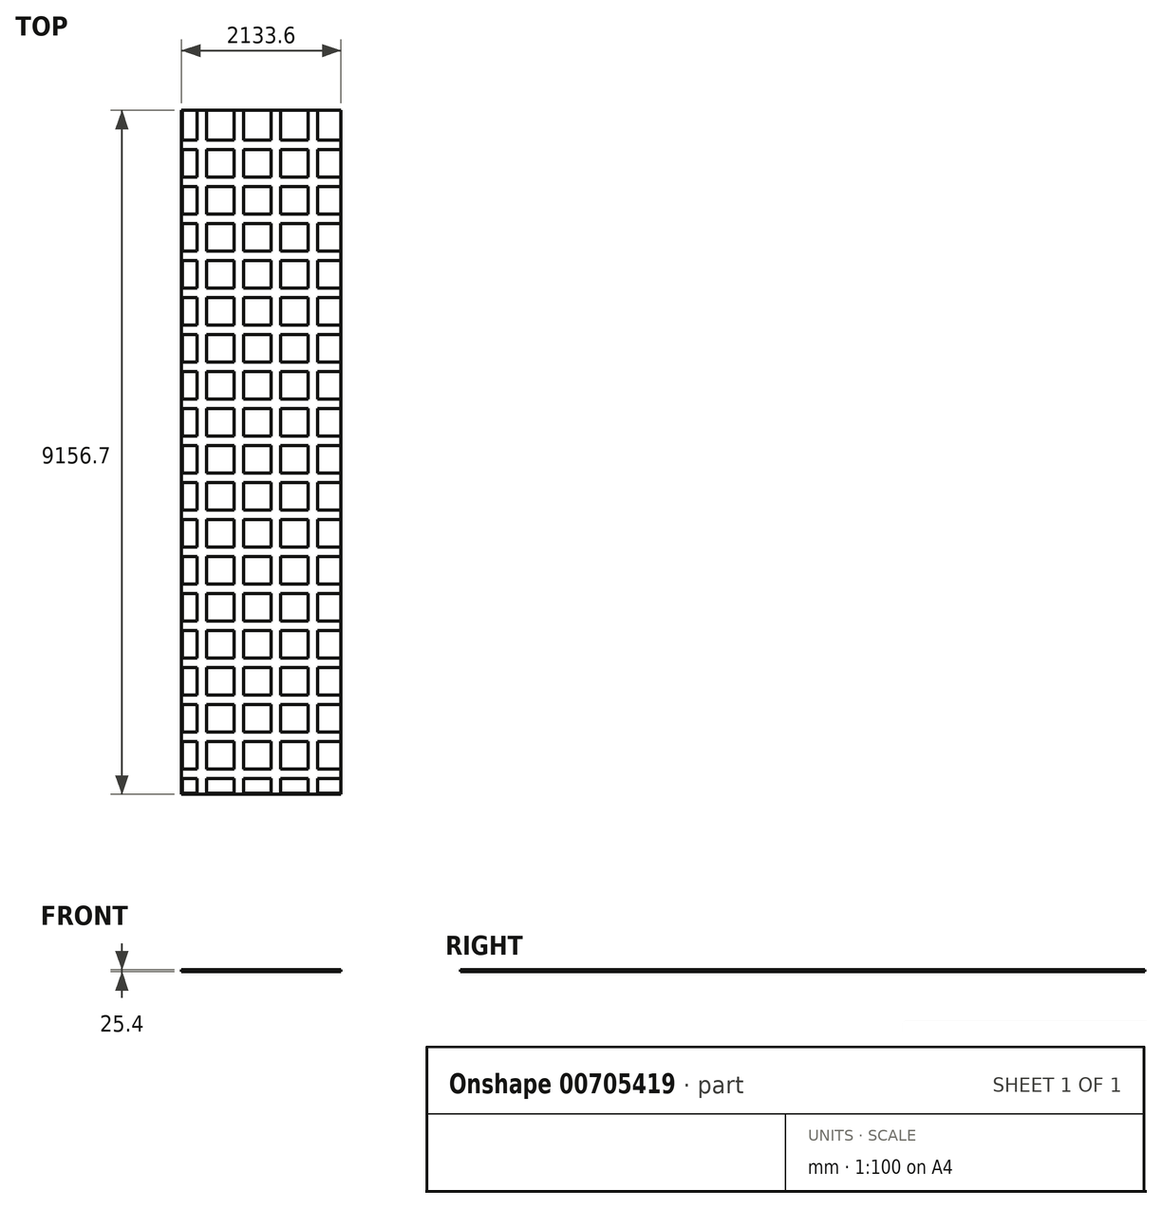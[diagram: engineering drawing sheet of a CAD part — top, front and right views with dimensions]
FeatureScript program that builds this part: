
annotation { "Feature Type Name" : "Feature", "Feature Type Description" : "" }
export const myFeature = defineFeature(function(context is Context, id is Id, definition is map)
    precondition{}
    {
        {
            var Q0;
            Q0=qCreatedBy(makeId("Top.planeOp"),FACE);
            var sketch = newSketch(context, id + "F0", { "sketchPlane" : qUnion([Q0])});
            skLineSegment(sketch, "E0.bottom", {"start": v(0, 0) * mm, "end": v(2133.6, 0) * mm});
            skLineSegment(sketch, "E0.top", {"start": v(0, 9156.7) * mm, "end": v(2133.6, 9156.7) * mm});
            skLineSegment(sketch, "E0.left", {"start": v(0, 0) * mm, "end": v(0, 9156.7) * mm});
            skLineSegment(sketch, "E0.right", {"start": v(2133.6, 0) * mm, "end": v(2133.6, 9156.7) * mm});
            skSolve(sketch);
        }
        {
            var Q0;
            Q0=makeQuery(id+"F0.imprint","IMPRINT",FACE,{"disambiguationData":[TD([[makeQuery(id+"F0.imprint","IMPRINT",EDGE,{"derivedFrom":sQuery(id+"F0.wireOp",EDGE,"E0.bottom")}),1.0]])]});
            extrude(context, id + "F1", {"entities" : qUnion([Q0]), "depth" : 25.4 * mm, "offsetDistance" : 25.4 * mm});
        }
        {
            var Q0;
            Q0=makeQuery(id+"F1.opExtrude","CAP_FACE",FACE,{"disambiguationData":[OSD([sQuery(id+"F0.wireOp",EDGE,"E0.bottom"),sQuery(id+"F0.wireOp",EDGE,"E0.top"),sQuery(id+"F0.wireOp",EDGE,"E0.left"),sQuery(id+"F0.wireOp",EDGE,"E0.right")])],"isStart":false});
            var sketch = newSketch(context, id + "F2", { "sketchPlane" : qUnion([Q0])});
            skLineSegment(sketch, "E1.0", {"start": v(12.7, 0) * mm, "end": v(12.7, 9156.7) * mm});
            skLineSegment(sketch, "E2", {"start": v(336.55, 12.7) * mm, "end": v(336.55, 9156.7) * mm});
            skLineSegment(sketch, "E3.0", {"start": v(0, 12.7) * mm, "end": v(2133.6, 12.7) * mm});
            skLineSegment(sketch, "E4", {"start": v(12.7, 336.55) * mm, "end": v(2133.6, 336.55) * mm});
            skLineSegment(sketch, "E5.0", {"start": v(209.55, 12.7) * mm, "end": v(209.55, 9156.7) * mm});
            skLineSegment(sketch, "E6.0", {"start": v(12.7, 209.55) * mm, "end": v(2133.6, 209.55) * mm});
            skLineSegment(sketch, "E7.1.0.0", {"start": v(704.85, 12.7) * mm, "end": v(704.85, 9156.7) * mm});
            skLineSegment(sketch, "E7.1.0.1", {"start": v(831.85, 12.7) * mm, "end": v(831.85, 9156.7) * mm});
            skLineSegment(sketch, "E7.2.0.0", {"start": v(1200.15, 12.7) * mm, "end": v(1200.15, 9156.7) * mm});
            skLineSegment(sketch, "E7.2.0.1", {"start": v(1327.15, 12.7) * mm, "end": v(1327.15, 9156.7) * mm});
            skLineSegment(sketch, "E7.3.0.0", {"start": v(1695.45, 12.7) * mm, "end": v(1695.45, 9156.7) * mm});
            skLineSegment(sketch, "E7.3.0.1", {"start": v(1822.45, 12.7) * mm, "end": v(1822.45, 9156.7) * mm});
            skLineSegment(sketch, "E7.direction1", {"start": v(209.55, 12.7) * mm, "end": v(704.85, 12.7) * mm, "construction": true});
            skLineSegment(sketch, "E8.0.1.0", {"start": v(12.7, 831.85) * mm, "end": v(2133.6, 831.85) * mm});
            skLineSegment(sketch, "E8.0.1.1", {"start": v(12.7, 704.85) * mm, "end": v(2133.6, 704.85) * mm});
            skLineSegment(sketch, "E8.0.2.0", {"start": v(12.7, 1327.15) * mm, "end": v(2133.6, 1327.15) * mm});
            skLineSegment(sketch, "E8.0.2.1", {"start": v(12.7, 1200.15) * mm, "end": v(2133.6, 1200.15) * mm});
            skLineSegment(sketch, "E8.0.3.0", {"start": v(12.7, 1822.45) * mm, "end": v(2133.6, 1822.45) * mm});
            skLineSegment(sketch, "E8.0.3.1", {"start": v(12.7, 1695.45) * mm, "end": v(2133.6, 1695.45) * mm});
            skLineSegment(sketch, "E8.0.4.0", {"start": v(12.7, 2317.75) * mm, "end": v(2133.6, 2317.75) * mm});
            skLineSegment(sketch, "E8.0.4.1", {"start": v(12.7, 2190.75) * mm, "end": v(2133.6, 2190.75) * mm});
            skLineSegment(sketch, "E8.0.5.0", {"start": v(12.7, 2813.05) * mm, "end": v(2133.6, 2813.05) * mm});
            skLineSegment(sketch, "E8.0.5.1", {"start": v(12.7, 2686.05) * mm, "end": v(2133.6, 2686.05) * mm});
            skLineSegment(sketch, "E8.0.6.0", {"start": v(12.7, 3308.35) * mm, "end": v(2133.6, 3308.35) * mm});
            skLineSegment(sketch, "E8.0.6.1", {"start": v(12.7, 3181.35) * mm, "end": v(2133.6, 3181.35) * mm});
            skLineSegment(sketch, "E8.0.7.0", {"start": v(12.7, 3803.65) * mm, "end": v(2133.6, 3803.65) * mm});
            skLineSegment(sketch, "E8.0.7.1", {"start": v(12.7, 3676.65) * mm, "end": v(2133.6, 3676.65) * mm});
            skLineSegment(sketch, "E8.0.8.0", {"start": v(12.7, 4298.95) * mm, "end": v(2133.6, 4298.95) * mm});
            skLineSegment(sketch, "E8.0.8.1", {"start": v(12.7, 4171.95) * mm, "end": v(2133.6, 4171.95) * mm});
            skLineSegment(sketch, "E8.0.9.0", {"start": v(12.7, 4794.25) * mm, "end": v(2133.6, 4794.25) * mm});
            skLineSegment(sketch, "E8.0.9.1", {"start": v(12.7, 4667.25) * mm, "end": v(2133.6, 4667.25) * mm});
            skLineSegment(sketch, "E8.0.10.0", {"start": v(12.7, 5289.55) * mm, "end": v(2133.6, 5289.55) * mm});
            skLineSegment(sketch, "E8.0.10.1", {"start": v(12.7, 5162.55) * mm, "end": v(2133.6, 5162.55) * mm});
            skLineSegment(sketch, "E8.0.11.0", {"start": v(12.7, 5784.85) * mm, "end": v(2133.6, 5784.85) * mm});
            skLineSegment(sketch, "E8.0.11.1", {"start": v(12.7, 5657.85) * mm, "end": v(2133.6, 5657.85) * mm});
            skLineSegment(sketch, "E8.0.12.0", {"start": v(12.7, 6280.15) * mm, "end": v(2133.6, 6280.15) * mm});
            skLineSegment(sketch, "E8.0.12.1", {"start": v(12.7, 6153.15) * mm, "end": v(2133.6, 6153.15) * mm});
            skLineSegment(sketch, "E8.0.13.0", {"start": v(12.7, 6775.45) * mm, "end": v(2133.6, 6775.45) * mm});
            skLineSegment(sketch, "E8.0.13.1", {"start": v(12.7, 6648.45) * mm, "end": v(2133.6, 6648.45) * mm});
            skLineSegment(sketch, "E8.0.14.0", {"start": v(12.7, 7270.75) * mm, "end": v(2133.6, 7270.75) * mm});
            skLineSegment(sketch, "E8.0.14.1", {"start": v(12.7, 7143.75) * mm, "end": v(2133.6, 7143.75) * mm});
            skLineSegment(sketch, "E8.0.15.0", {"start": v(12.7, 7766.05) * mm, "end": v(2133.6, 7766.05) * mm});
            skLineSegment(sketch, "E8.0.15.1", {"start": v(12.7, 7639.05) * mm, "end": v(2133.6, 7639.05) * mm});
            skLineSegment(sketch, "E8.0.16.0", {"start": v(12.7, 8261.35) * mm, "end": v(2133.6, 8261.35) * mm});
            skLineSegment(sketch, "E8.0.16.1", {"start": v(12.7, 8134.35) * mm, "end": v(2133.6, 8134.35) * mm});
            skLineSegment(sketch, "E8.0.17.0", {"start": v(12.7, 8756.65) * mm, "end": v(2133.6, 8756.65) * mm});
            skLineSegment(sketch, "E8.0.17.1", {"start": v(12.7, 8629.65) * mm, "end": v(2133.6, 8629.65) * mm});
            skLineSegment(sketch, "E8.direction1", {"start": v(12.7, 336.55) * mm, "end": v(38.1, 336.55) * mm, "construction": true});
            skLineSegment(sketch, "E8.direction2", {"start": v(12.7, 336.55) * mm, "end": v(12.7, 831.85) * mm, "construction": true});
            skLineSegment(sketch, "E9.3.0.18", {"start": v(12.7, 9124.95) * mm, "end": v(2133.6, 9124.95) * mm});
            skSolve(sketch);
        }
        {
            var Q0;
            {var subQ0=sQuery(id+"F2.wireOp",EDGE,"E4");var subQ1=sQuery(id+"F2.wireOp",EDGE,"E1.0");var subQ2=makeQuery(id+"F2.imprint","INTERSECT",VERTEX,{"derivedFrom":[subQ1,subQ0]});Q0=makeQuery(id+"F2.imprint","IMPRINT",FACE,{"disambiguationData":[TD([[makeQuery(id+"F2.imprint","IMPRINT",EDGE,{"disambiguationData":[TD([[subQ2,-1.0]])],"derivedFrom":subQ1}),-1.0]])]});}
            var Q1;
            {var subQ0=sQuery(id+"F2.wireOp",EDGE,"E4");var subQ1=sQuery(id+"F2.wireOp",EDGE,"E2");var subQ2=makeQuery(id+"F2.imprint","INTERSECT",VERTEX,{"derivedFrom":[subQ1,subQ0]});Q1=makeQuery(id+"F2.imprint","IMPRINT",FACE,{"disambiguationData":[TD([[makeQuery(id+"F2.imprint","IMPRINT",EDGE,{"disambiguationData":[TD([[subQ2,-1.0]])],"derivedFrom":subQ1}),-1.0]])]});}
            var Q2;
            {var subQ0=sQuery(id+"F2.wireOp",EDGE,"E7.1.0.1");var subQ1=sQuery(id+"F2.wireOp",EDGE,"E4");var subQ2=makeQuery(id+"F2.imprint","INTERSECT",VERTEX,{"derivedFrom":[subQ1,subQ0]});Q2=makeQuery(id+"F2.imprint","IMPRINT",FACE,{"disambiguationData":[TD([[makeQuery(id+"F2.imprint","IMPRINT",EDGE,{"disambiguationData":[TD([[subQ2,-1.0]])],"derivedFrom":subQ1}),1.0]])]});}
            var Q3;
            {var subQ0=sQuery(id+"F2.wireOp",EDGE,"E7.2.0.1");var subQ1=sQuery(id+"F2.wireOp",EDGE,"E4");var subQ2=makeQuery(id+"F2.imprint","INTERSECT",VERTEX,{"derivedFrom":[subQ1,subQ0]});Q3=makeQuery(id+"F2.imprint","IMPRINT",FACE,{"disambiguationData":[TD([[makeQuery(id+"F2.imprint","IMPRINT",EDGE,{"disambiguationData":[TD([[subQ2,-1.0]])],"derivedFrom":subQ1}),1.0]])]});}
            var Q4;
            {var subQ0=sQuery(id+"F2.wireOp",EDGE,"E4");var subQ1=makeQuery(id+"F1.opExtrude","CAP_EDGE",EDGE,{"disambiguationData":[OSD([sQuery(id+"F0.wireOp",EDGE,"E0.right")])],"isStart":false});var subQ2=makeQuery(id+"F2.imprint","INTERSECT",VERTEX,{"derivedFrom":[subQ1,subQ0]});Q4=makeQuery(id+"F2.imprint","IMPRINT",FACE,{"disambiguationData":[TD([[makeQuery(id+"F2.imprint","IMPRINT",EDGE,{"disambiguationData":[TD([[subQ2,1.0]])],"derivedFrom":subQ0}),1.0]])]});}
            var Q5;
            {var subQ0=sQuery(id+"F2.wireOp",EDGE,"E8.0.1.0");var subQ1=sQuery(id+"F2.wireOp",EDGE,"E1.0");var subQ2=makeQuery(id+"F2.imprint","INTERSECT",VERTEX,{"derivedFrom":[subQ1,subQ0]});Q5=makeQuery(id+"F2.imprint","IMPRINT",FACE,{"disambiguationData":[TD([[makeQuery(id+"F2.imprint","IMPRINT",EDGE,{"disambiguationData":[TD([[subQ2,-1.0]])],"derivedFrom":subQ1}),-1.0]])]});}
            var Q6;
            {var subQ0=sQuery(id+"F2.wireOp",EDGE,"E8.0.1.0");var subQ1=sQuery(id+"F2.wireOp",EDGE,"E2");var subQ2=makeQuery(id+"F2.imprint","INTERSECT",VERTEX,{"derivedFrom":[subQ1,subQ0]});Q6=makeQuery(id+"F2.imprint","IMPRINT",FACE,{"disambiguationData":[TD([[makeQuery(id+"F2.imprint","IMPRINT",EDGE,{"disambiguationData":[TD([[subQ2,-1.0]])],"derivedFrom":subQ1}),-1.0]])]});}
            var Q7;
            {var subQ0=sQuery(id+"F2.wireOp",EDGE,"E8.0.1.0");var subQ1=sQuery(id+"F2.wireOp",EDGE,"E7.1.0.1");var subQ2=makeQuery(id+"F2.imprint","INTERSECT",VERTEX,{"derivedFrom":[subQ1,subQ0]});Q7=makeQuery(id+"F2.imprint","IMPRINT",FACE,{"disambiguationData":[TD([[makeQuery(id+"F2.imprint","IMPRINT",EDGE,{"disambiguationData":[TD([[subQ2,-1.0]])],"derivedFrom":subQ1}),-1.0]])]});}
            var Q8;
            {var subQ0=sQuery(id+"F2.wireOp",EDGE,"E8.0.1.0");var subQ1=sQuery(id+"F2.wireOp",EDGE,"E7.2.0.1");var subQ2=makeQuery(id+"F2.imprint","INTERSECT",VERTEX,{"derivedFrom":[subQ1,subQ0]});Q8=makeQuery(id+"F2.imprint","IMPRINT",FACE,{"disambiguationData":[TD([[makeQuery(id+"F2.imprint","IMPRINT",EDGE,{"disambiguationData":[TD([[subQ2,-1.0]])],"derivedFrom":subQ1}),-1.0]])]});}
            var Q9;
            {var subQ0=sQuery(id+"F2.wireOp",EDGE,"E8.0.1.0");var subQ1=sQuery(id+"F2.wireOp",EDGE,"E7.3.0.1");var subQ2=makeQuery(id+"F2.imprint","INTERSECT",VERTEX,{"derivedFrom":[subQ1,subQ0]});Q9=makeQuery(id+"F2.imprint","IMPRINT",FACE,{"disambiguationData":[TD([[makeQuery(id+"F2.imprint","IMPRINT",EDGE,{"disambiguationData":[TD([[subQ2,-1.0]])],"derivedFrom":subQ1}),-1.0]])]});}
            var Q10;
            {var subQ0=sQuery(id+"F2.wireOp",EDGE,"E8.0.2.0");var subQ1=sQuery(id+"F2.wireOp",EDGE,"E7.3.0.1");var subQ2=makeQuery(id+"F2.imprint","INTERSECT",VERTEX,{"derivedFrom":[subQ1,subQ0]});Q10=makeQuery(id+"F2.imprint","IMPRINT",FACE,{"disambiguationData":[TD([[makeQuery(id+"F2.imprint","IMPRINT",EDGE,{"disambiguationData":[TD([[subQ2,-1.0]])],"derivedFrom":subQ1}),-1.0]])]});}
            var Q11;
            {var subQ0=sQuery(id+"F2.wireOp",EDGE,"E8.0.2.0");var subQ1=sQuery(id+"F2.wireOp",EDGE,"E7.2.0.1");var subQ2=makeQuery(id+"F2.imprint","INTERSECT",VERTEX,{"derivedFrom":[subQ1,subQ0]});Q11=makeQuery(id+"F2.imprint","IMPRINT",FACE,{"disambiguationData":[TD([[makeQuery(id+"F2.imprint","IMPRINT",EDGE,{"disambiguationData":[TD([[subQ2,-1.0]])],"derivedFrom":subQ1}),-1.0]])]});}
            var Q12;
            {var subQ0=sQuery(id+"F2.wireOp",EDGE,"E8.0.2.0");var subQ1=sQuery(id+"F2.wireOp",EDGE,"E7.1.0.1");var subQ2=makeQuery(id+"F2.imprint","INTERSECT",VERTEX,{"derivedFrom":[subQ1,subQ0]});Q12=makeQuery(id+"F2.imprint","IMPRINT",FACE,{"disambiguationData":[TD([[makeQuery(id+"F2.imprint","IMPRINT",EDGE,{"disambiguationData":[TD([[subQ2,-1.0]])],"derivedFrom":subQ1}),-1.0]])]});}
            var Q13;
            {var subQ0=sQuery(id+"F2.wireOp",EDGE,"E8.0.2.0");var subQ1=sQuery(id+"F2.wireOp",EDGE,"E2");var subQ2=makeQuery(id+"F2.imprint","INTERSECT",VERTEX,{"derivedFrom":[subQ1,subQ0]});Q13=makeQuery(id+"F2.imprint","IMPRINT",FACE,{"disambiguationData":[TD([[makeQuery(id+"F2.imprint","IMPRINT",EDGE,{"disambiguationData":[TD([[subQ2,-1.0]])],"derivedFrom":subQ1}),-1.0]])]});}
            var Q14;
            {var subQ0=sQuery(id+"F2.wireOp",EDGE,"E8.0.2.0");var subQ1=sQuery(id+"F2.wireOp",EDGE,"E1.0");var subQ2=makeQuery(id+"F2.imprint","INTERSECT",VERTEX,{"derivedFrom":[subQ1,subQ0]});Q14=makeQuery(id+"F2.imprint","IMPRINT",FACE,{"disambiguationData":[TD([[makeQuery(id+"F2.imprint","IMPRINT",EDGE,{"disambiguationData":[TD([[subQ2,-1.0]])],"derivedFrom":subQ1}),-1.0]])]});}
            var Q15;
            {var subQ0=sQuery(id+"F2.wireOp",EDGE,"E8.0.3.0");var subQ1=sQuery(id+"F2.wireOp",EDGE,"E1.0");var subQ2=makeQuery(id+"F2.imprint","INTERSECT",VERTEX,{"derivedFrom":[subQ1,subQ0]});Q15=makeQuery(id+"F2.imprint","IMPRINT",FACE,{"disambiguationData":[TD([[makeQuery(id+"F2.imprint","IMPRINT",EDGE,{"disambiguationData":[TD([[subQ2,-1.0]])],"derivedFrom":subQ1}),-1.0]])]});}
            var Q16;
            {var subQ0=sQuery(id+"F2.wireOp",EDGE,"E8.0.3.0");var subQ1=sQuery(id+"F2.wireOp",EDGE,"E2");var subQ2=makeQuery(id+"F2.imprint","INTERSECT",VERTEX,{"derivedFrom":[subQ1,subQ0]});Q16=makeQuery(id+"F2.imprint","IMPRINT",FACE,{"disambiguationData":[TD([[makeQuery(id+"F2.imprint","IMPRINT",EDGE,{"disambiguationData":[TD([[subQ2,-1.0]])],"derivedFrom":subQ1}),-1.0]])]});}
            var Q17;
            {var subQ0=sQuery(id+"F2.wireOp",EDGE,"E8.0.3.0");var subQ1=sQuery(id+"F2.wireOp",EDGE,"E7.1.0.1");var subQ2=makeQuery(id+"F2.imprint","INTERSECT",VERTEX,{"derivedFrom":[subQ1,subQ0]});Q17=makeQuery(id+"F2.imprint","IMPRINT",FACE,{"disambiguationData":[TD([[makeQuery(id+"F2.imprint","IMPRINT",EDGE,{"disambiguationData":[TD([[subQ2,-1.0]])],"derivedFrom":subQ1}),-1.0]])]});}
            var Q18;
            {var subQ0=sQuery(id+"F2.wireOp",EDGE,"E8.0.3.0");var subQ1=sQuery(id+"F2.wireOp",EDGE,"E7.2.0.1");var subQ2=makeQuery(id+"F2.imprint","INTERSECT",VERTEX,{"derivedFrom":[subQ1,subQ0]});Q18=makeQuery(id+"F2.imprint","IMPRINT",FACE,{"disambiguationData":[TD([[makeQuery(id+"F2.imprint","IMPRINT",EDGE,{"disambiguationData":[TD([[subQ2,-1.0]])],"derivedFrom":subQ1}),-1.0]])]});}
            var Q19;
            {var subQ0=sQuery(id+"F2.wireOp",EDGE,"E8.0.3.0");var subQ1=sQuery(id+"F2.wireOp",EDGE,"E7.3.0.1");var subQ2=makeQuery(id+"F2.imprint","INTERSECT",VERTEX,{"derivedFrom":[subQ1,subQ0]});Q19=makeQuery(id+"F2.imprint","IMPRINT",FACE,{"disambiguationData":[TD([[makeQuery(id+"F2.imprint","IMPRINT",EDGE,{"disambiguationData":[TD([[subQ2,-1.0]])],"derivedFrom":subQ1}),-1.0]])]});}
            var Q20;
            {var subQ0=sQuery(id+"F2.wireOp",EDGE,"E8.0.4.0");var subQ1=sQuery(id+"F2.wireOp",EDGE,"E7.3.0.1");var subQ2=makeQuery(id+"F2.imprint","INTERSECT",VERTEX,{"derivedFrom":[subQ1,subQ0]});Q20=makeQuery(id+"F2.imprint","IMPRINT",FACE,{"disambiguationData":[TD([[makeQuery(id+"F2.imprint","IMPRINT",EDGE,{"disambiguationData":[TD([[subQ2,-1.0]])],"derivedFrom":subQ1}),-1.0]])]});}
            var Q21;
            {var subQ0=sQuery(id+"F2.wireOp",EDGE,"E8.0.4.0");var subQ1=sQuery(id+"F2.wireOp",EDGE,"E7.2.0.1");var subQ2=makeQuery(id+"F2.imprint","INTERSECT",VERTEX,{"derivedFrom":[subQ1,subQ0]});Q21=makeQuery(id+"F2.imprint","IMPRINT",FACE,{"disambiguationData":[TD([[makeQuery(id+"F2.imprint","IMPRINT",EDGE,{"disambiguationData":[TD([[subQ2,-1.0]])],"derivedFrom":subQ1}),-1.0]])]});}
            var Q22;
            {var subQ0=sQuery(id+"F2.wireOp",EDGE,"E8.0.4.0");var subQ1=sQuery(id+"F2.wireOp",EDGE,"E7.1.0.1");var subQ2=makeQuery(id+"F2.imprint","INTERSECT",VERTEX,{"derivedFrom":[subQ1,subQ0]});Q22=makeQuery(id+"F2.imprint","IMPRINT",FACE,{"disambiguationData":[TD([[makeQuery(id+"F2.imprint","IMPRINT",EDGE,{"disambiguationData":[TD([[subQ2,-1.0]])],"derivedFrom":subQ1}),-1.0]])]});}
            var Q23;
            {var subQ0=sQuery(id+"F2.wireOp",EDGE,"E8.0.4.0");var subQ1=sQuery(id+"F2.wireOp",EDGE,"E2");var subQ2=makeQuery(id+"F2.imprint","INTERSECT",VERTEX,{"derivedFrom":[subQ1,subQ0]});Q23=makeQuery(id+"F2.imprint","IMPRINT",FACE,{"disambiguationData":[TD([[makeQuery(id+"F2.imprint","IMPRINT",EDGE,{"disambiguationData":[TD([[subQ2,-1.0]])],"derivedFrom":subQ1}),-1.0]])]});}
            var Q24;
            {var subQ0=sQuery(id+"F2.wireOp",EDGE,"E8.0.4.0");var subQ1=sQuery(id+"F2.wireOp",EDGE,"E1.0");var subQ2=makeQuery(id+"F2.imprint","INTERSECT",VERTEX,{"derivedFrom":[subQ1,subQ0]});Q24=makeQuery(id+"F2.imprint","IMPRINT",FACE,{"disambiguationData":[TD([[makeQuery(id+"F2.imprint","IMPRINT",EDGE,{"disambiguationData":[TD([[subQ2,-1.0]])],"derivedFrom":subQ1}),-1.0]])]});}
            var Q25;
            {var subQ0=sQuery(id+"F2.wireOp",EDGE,"E8.0.5.0");var subQ1=sQuery(id+"F2.wireOp",EDGE,"E1.0");var subQ2=makeQuery(id+"F2.imprint","INTERSECT",VERTEX,{"derivedFrom":[subQ1,subQ0]});Q25=makeQuery(id+"F2.imprint","IMPRINT",FACE,{"disambiguationData":[TD([[makeQuery(id+"F2.imprint","IMPRINT",EDGE,{"disambiguationData":[TD([[subQ2,-1.0]])],"derivedFrom":subQ1}),-1.0]])]});}
            var Q26;
            {var subQ0=sQuery(id+"F2.wireOp",EDGE,"E8.0.5.0");var subQ1=sQuery(id+"F2.wireOp",EDGE,"E2");var subQ2=makeQuery(id+"F2.imprint","INTERSECT",VERTEX,{"derivedFrom":[subQ1,subQ0]});Q26=makeQuery(id+"F2.imprint","IMPRINT",FACE,{"disambiguationData":[TD([[makeQuery(id+"F2.imprint","IMPRINT",EDGE,{"disambiguationData":[TD([[subQ2,-1.0]])],"derivedFrom":subQ1}),-1.0]])]});}
            var Q27;
            {var subQ0=sQuery(id+"F2.wireOp",EDGE,"E8.0.5.0");var subQ1=sQuery(id+"F2.wireOp",EDGE,"E7.1.0.1");var subQ2=makeQuery(id+"F2.imprint","INTERSECT",VERTEX,{"derivedFrom":[subQ1,subQ0]});Q27=makeQuery(id+"F2.imprint","IMPRINT",FACE,{"disambiguationData":[TD([[makeQuery(id+"F2.imprint","IMPRINT",EDGE,{"disambiguationData":[TD([[subQ2,-1.0]])],"derivedFrom":subQ1}),-1.0]])]});}
            var Q28;
            {var subQ0=sQuery(id+"F2.wireOp",EDGE,"E8.0.5.0");var subQ1=sQuery(id+"F2.wireOp",EDGE,"E7.2.0.1");var subQ2=makeQuery(id+"F2.imprint","INTERSECT",VERTEX,{"derivedFrom":[subQ1,subQ0]});Q28=makeQuery(id+"F2.imprint","IMPRINT",FACE,{"disambiguationData":[TD([[makeQuery(id+"F2.imprint","IMPRINT",EDGE,{"disambiguationData":[TD([[subQ2,-1.0]])],"derivedFrom":subQ1}),-1.0]])]});}
            var Q29;
            {var subQ0=sQuery(id+"F2.wireOp",EDGE,"E8.0.5.0");var subQ1=sQuery(id+"F2.wireOp",EDGE,"E7.3.0.1");var subQ2=makeQuery(id+"F2.imprint","INTERSECT",VERTEX,{"derivedFrom":[subQ1,subQ0]});Q29=makeQuery(id+"F2.imprint","IMPRINT",FACE,{"disambiguationData":[TD([[makeQuery(id+"F2.imprint","IMPRINT",EDGE,{"disambiguationData":[TD([[subQ2,-1.0]])],"derivedFrom":subQ1}),-1.0]])]});}
            var Q30;
            {var subQ0=sQuery(id+"F2.wireOp",EDGE,"E8.0.6.0");var subQ1=sQuery(id+"F2.wireOp",EDGE,"E7.3.0.1");var subQ2=makeQuery(id+"F2.imprint","INTERSECT",VERTEX,{"derivedFrom":[subQ1,subQ0]});Q30=makeQuery(id+"F2.imprint","IMPRINT",FACE,{"disambiguationData":[TD([[makeQuery(id+"F2.imprint","IMPRINT",EDGE,{"disambiguationData":[TD([[subQ2,-1.0]])],"derivedFrom":subQ1}),-1.0]])]});}
            var Q31;
            {var subQ0=sQuery(id+"F2.wireOp",EDGE,"E8.0.6.0");var subQ1=sQuery(id+"F2.wireOp",EDGE,"E7.2.0.1");var subQ2=makeQuery(id+"F2.imprint","INTERSECT",VERTEX,{"derivedFrom":[subQ1,subQ0]});Q31=makeQuery(id+"F2.imprint","IMPRINT",FACE,{"disambiguationData":[TD([[makeQuery(id+"F2.imprint","IMPRINT",EDGE,{"disambiguationData":[TD([[subQ2,-1.0]])],"derivedFrom":subQ1}),-1.0]])]});}
            var Q32;
            {var subQ0=sQuery(id+"F2.wireOp",EDGE,"E8.0.6.0");var subQ1=sQuery(id+"F2.wireOp",EDGE,"E7.1.0.1");var subQ2=makeQuery(id+"F2.imprint","INTERSECT",VERTEX,{"derivedFrom":[subQ1,subQ0]});Q32=makeQuery(id+"F2.imprint","IMPRINT",FACE,{"disambiguationData":[TD([[makeQuery(id+"F2.imprint","IMPRINT",EDGE,{"disambiguationData":[TD([[subQ2,-1.0]])],"derivedFrom":subQ1}),-1.0]])]});}
            var Q33;
            {var subQ0=sQuery(id+"F2.wireOp",EDGE,"E8.0.6.0");var subQ1=sQuery(id+"F2.wireOp",EDGE,"E2");var subQ2=makeQuery(id+"F2.imprint","INTERSECT",VERTEX,{"derivedFrom":[subQ1,subQ0]});Q33=makeQuery(id+"F2.imprint","IMPRINT",FACE,{"disambiguationData":[TD([[makeQuery(id+"F2.imprint","IMPRINT",EDGE,{"disambiguationData":[TD([[subQ2,-1.0]])],"derivedFrom":subQ1}),-1.0]])]});}
            var Q34;
            {var subQ0=sQuery(id+"F2.wireOp",EDGE,"E8.0.6.0");var subQ1=sQuery(id+"F2.wireOp",EDGE,"E1.0");var subQ2=makeQuery(id+"F2.imprint","INTERSECT",VERTEX,{"derivedFrom":[subQ1,subQ0]});Q34=makeQuery(id+"F2.imprint","IMPRINT",FACE,{"disambiguationData":[TD([[makeQuery(id+"F2.imprint","IMPRINT",EDGE,{"disambiguationData":[TD([[subQ2,-1.0]])],"derivedFrom":subQ1}),-1.0]])]});}
            var Q35;
            {var subQ0=sQuery(id+"F2.wireOp",EDGE,"E8.0.7.0");var subQ1=sQuery(id+"F2.wireOp",EDGE,"E1.0");var subQ2=makeQuery(id+"F2.imprint","INTERSECT",VERTEX,{"derivedFrom":[subQ1,subQ0]});Q35=makeQuery(id+"F2.imprint","IMPRINT",FACE,{"disambiguationData":[TD([[makeQuery(id+"F2.imprint","IMPRINT",EDGE,{"disambiguationData":[TD([[subQ2,-1.0]])],"derivedFrom":subQ1}),-1.0]])]});}
            var Q36;
            {var subQ0=sQuery(id+"F2.wireOp",EDGE,"E8.0.7.0");var subQ1=sQuery(id+"F2.wireOp",EDGE,"E2");var subQ2=makeQuery(id+"F2.imprint","INTERSECT",VERTEX,{"derivedFrom":[subQ1,subQ0]});Q36=makeQuery(id+"F2.imprint","IMPRINT",FACE,{"disambiguationData":[TD([[makeQuery(id+"F2.imprint","IMPRINT",EDGE,{"disambiguationData":[TD([[subQ2,-1.0]])],"derivedFrom":subQ1}),-1.0]])]});}
            var Q37;
            {var subQ0=sQuery(id+"F2.wireOp",EDGE,"E8.0.7.0");var subQ1=sQuery(id+"F2.wireOp",EDGE,"E7.1.0.1");var subQ2=makeQuery(id+"F2.imprint","INTERSECT",VERTEX,{"derivedFrom":[subQ1,subQ0]});Q37=makeQuery(id+"F2.imprint","IMPRINT",FACE,{"disambiguationData":[TD([[makeQuery(id+"F2.imprint","IMPRINT",EDGE,{"disambiguationData":[TD([[subQ2,-1.0]])],"derivedFrom":subQ1}),-1.0]])]});}
            var Q38;
            {var subQ0=sQuery(id+"F2.wireOp",EDGE,"E8.0.7.0");var subQ1=sQuery(id+"F2.wireOp",EDGE,"E7.2.0.1");var subQ2=makeQuery(id+"F2.imprint","INTERSECT",VERTEX,{"derivedFrom":[subQ1,subQ0]});Q38=makeQuery(id+"F2.imprint","IMPRINT",FACE,{"disambiguationData":[TD([[makeQuery(id+"F2.imprint","IMPRINT",EDGE,{"disambiguationData":[TD([[subQ2,-1.0]])],"derivedFrom":subQ1}),-1.0]])]});}
            var Q39;
            {var subQ0=sQuery(id+"F2.wireOp",EDGE,"E8.0.7.0");var subQ1=sQuery(id+"F2.wireOp",EDGE,"E7.3.0.1");var subQ2=makeQuery(id+"F2.imprint","INTERSECT",VERTEX,{"derivedFrom":[subQ1,subQ0]});Q39=makeQuery(id+"F2.imprint","IMPRINT",FACE,{"disambiguationData":[TD([[makeQuery(id+"F2.imprint","IMPRINT",EDGE,{"disambiguationData":[TD([[subQ2,-1.0]])],"derivedFrom":subQ1}),-1.0]])]});}
            var Q40;
            {var subQ0=sQuery(id+"F2.wireOp",EDGE,"E8.0.8.0");var subQ1=sQuery(id+"F2.wireOp",EDGE,"E7.3.0.1");var subQ2=makeQuery(id+"F2.imprint","INTERSECT",VERTEX,{"derivedFrom":[subQ1,subQ0]});Q40=makeQuery(id+"F2.imprint","IMPRINT",FACE,{"disambiguationData":[TD([[makeQuery(id+"F2.imprint","IMPRINT",EDGE,{"disambiguationData":[TD([[subQ2,-1.0]])],"derivedFrom":subQ1}),-1.0]])]});}
            var Q41;
            {var subQ0=sQuery(id+"F2.wireOp",EDGE,"E8.0.8.0");var subQ1=sQuery(id+"F2.wireOp",EDGE,"E7.2.0.1");var subQ2=makeQuery(id+"F2.imprint","INTERSECT",VERTEX,{"derivedFrom":[subQ1,subQ0]});Q41=makeQuery(id+"F2.imprint","IMPRINT",FACE,{"disambiguationData":[TD([[makeQuery(id+"F2.imprint","IMPRINT",EDGE,{"disambiguationData":[TD([[subQ2,-1.0]])],"derivedFrom":subQ1}),-1.0]])]});}
            var Q42;
            {var subQ0=sQuery(id+"F2.wireOp",EDGE,"E8.0.8.0");var subQ1=sQuery(id+"F2.wireOp",EDGE,"E7.1.0.1");var subQ2=makeQuery(id+"F2.imprint","INTERSECT",VERTEX,{"derivedFrom":[subQ1,subQ0]});Q42=makeQuery(id+"F2.imprint","IMPRINT",FACE,{"disambiguationData":[TD([[makeQuery(id+"F2.imprint","IMPRINT",EDGE,{"disambiguationData":[TD([[subQ2,-1.0]])],"derivedFrom":subQ1}),-1.0]])]});}
            var Q43;
            {var subQ0=sQuery(id+"F2.wireOp",EDGE,"E8.0.8.0");var subQ1=sQuery(id+"F2.wireOp",EDGE,"E2");var subQ2=makeQuery(id+"F2.imprint","INTERSECT",VERTEX,{"derivedFrom":[subQ1,subQ0]});Q43=makeQuery(id+"F2.imprint","IMPRINT",FACE,{"disambiguationData":[TD([[makeQuery(id+"F2.imprint","IMPRINT",EDGE,{"disambiguationData":[TD([[subQ2,-1.0]])],"derivedFrom":subQ1}),-1.0]])]});}
            var Q44;
            {var subQ0=sQuery(id+"F2.wireOp",EDGE,"E8.0.8.0");var subQ1=sQuery(id+"F2.wireOp",EDGE,"E1.0");var subQ2=makeQuery(id+"F2.imprint","INTERSECT",VERTEX,{"derivedFrom":[subQ1,subQ0]});Q44=makeQuery(id+"F2.imprint","IMPRINT",FACE,{"disambiguationData":[TD([[makeQuery(id+"F2.imprint","IMPRINT",EDGE,{"disambiguationData":[TD([[subQ2,-1.0]])],"derivedFrom":subQ1}),-1.0]])]});}
            var Q45;
            {var subQ0=sQuery(id+"F2.wireOp",EDGE,"E8.0.9.0");var subQ1=sQuery(id+"F2.wireOp",EDGE,"E1.0");var subQ2=makeQuery(id+"F2.imprint","INTERSECT",VERTEX,{"derivedFrom":[subQ1,subQ0]});Q45=makeQuery(id+"F2.imprint","IMPRINT",FACE,{"disambiguationData":[TD([[makeQuery(id+"F2.imprint","IMPRINT",EDGE,{"disambiguationData":[TD([[subQ2,-1.0]])],"derivedFrom":subQ1}),-1.0]])]});}
            var Q46;
            {var subQ0=sQuery(id+"F2.wireOp",EDGE,"E8.0.9.0");var subQ1=sQuery(id+"F2.wireOp",EDGE,"E2");var subQ2=makeQuery(id+"F2.imprint","INTERSECT",VERTEX,{"derivedFrom":[subQ1,subQ0]});Q46=makeQuery(id+"F2.imprint","IMPRINT",FACE,{"disambiguationData":[TD([[makeQuery(id+"F2.imprint","IMPRINT",EDGE,{"disambiguationData":[TD([[subQ2,-1.0]])],"derivedFrom":subQ1}),-1.0]])]});}
            var Q47;
            {var subQ0=sQuery(id+"F2.wireOp",EDGE,"E8.0.9.0");var subQ1=sQuery(id+"F2.wireOp",EDGE,"E7.1.0.1");var subQ2=makeQuery(id+"F2.imprint","INTERSECT",VERTEX,{"derivedFrom":[subQ1,subQ0]});Q47=makeQuery(id+"F2.imprint","IMPRINT",FACE,{"disambiguationData":[TD([[makeQuery(id+"F2.imprint","IMPRINT",EDGE,{"disambiguationData":[TD([[subQ2,-1.0]])],"derivedFrom":subQ1}),-1.0]])]});}
            var Q48;
            {var subQ0=sQuery(id+"F2.wireOp",EDGE,"E8.0.9.0");var subQ1=sQuery(id+"F2.wireOp",EDGE,"E7.2.0.1");var subQ2=makeQuery(id+"F2.imprint","INTERSECT",VERTEX,{"derivedFrom":[subQ1,subQ0]});Q48=makeQuery(id+"F2.imprint","IMPRINT",FACE,{"disambiguationData":[TD([[makeQuery(id+"F2.imprint","IMPRINT",EDGE,{"disambiguationData":[TD([[subQ2,-1.0]])],"derivedFrom":subQ1}),-1.0]])]});}
            var Q49;
            {var subQ0=sQuery(id+"F2.wireOp",EDGE,"E8.0.9.0");var subQ1=sQuery(id+"F2.wireOp",EDGE,"E7.3.0.1");var subQ2=makeQuery(id+"F2.imprint","INTERSECT",VERTEX,{"derivedFrom":[subQ1,subQ0]});Q49=makeQuery(id+"F2.imprint","IMPRINT",FACE,{"disambiguationData":[TD([[makeQuery(id+"F2.imprint","IMPRINT",EDGE,{"disambiguationData":[TD([[subQ2,-1.0]])],"derivedFrom":subQ1}),-1.0]])]});}
            var Q50;
            {var subQ0=sQuery(id+"F2.wireOp",EDGE,"E8.0.10.0");var subQ1=sQuery(id+"F2.wireOp",EDGE,"E7.3.0.1");var subQ2=makeQuery(id+"F2.imprint","INTERSECT",VERTEX,{"derivedFrom":[subQ1,subQ0]});Q50=makeQuery(id+"F2.imprint","IMPRINT",FACE,{"disambiguationData":[TD([[makeQuery(id+"F2.imprint","IMPRINT",EDGE,{"disambiguationData":[TD([[subQ2,-1.0]])],"derivedFrom":subQ1}),-1.0]])]});}
            var Q51;
            {var subQ0=sQuery(id+"F2.wireOp",EDGE,"E8.0.10.0");var subQ1=sQuery(id+"F2.wireOp",EDGE,"E7.2.0.1");var subQ2=makeQuery(id+"F2.imprint","INTERSECT",VERTEX,{"derivedFrom":[subQ1,subQ0]});Q51=makeQuery(id+"F2.imprint","IMPRINT",FACE,{"disambiguationData":[TD([[makeQuery(id+"F2.imprint","IMPRINT",EDGE,{"disambiguationData":[TD([[subQ2,-1.0]])],"derivedFrom":subQ1}),-1.0]])]});}
            var Q52;
            {var subQ0=sQuery(id+"F2.wireOp",EDGE,"E8.0.10.0");var subQ1=sQuery(id+"F2.wireOp",EDGE,"E7.1.0.1");var subQ2=makeQuery(id+"F2.imprint","INTERSECT",VERTEX,{"derivedFrom":[subQ1,subQ0]});Q52=makeQuery(id+"F2.imprint","IMPRINT",FACE,{"disambiguationData":[TD([[makeQuery(id+"F2.imprint","IMPRINT",EDGE,{"disambiguationData":[TD([[subQ2,-1.0]])],"derivedFrom":subQ1}),-1.0]])]});}
            var Q53;
            {var subQ0=sQuery(id+"F2.wireOp",EDGE,"E8.0.10.0");var subQ1=sQuery(id+"F2.wireOp",EDGE,"E2");var subQ2=makeQuery(id+"F2.imprint","INTERSECT",VERTEX,{"derivedFrom":[subQ1,subQ0]});Q53=makeQuery(id+"F2.imprint","IMPRINT",FACE,{"disambiguationData":[TD([[makeQuery(id+"F2.imprint","IMPRINT",EDGE,{"disambiguationData":[TD([[subQ2,-1.0]])],"derivedFrom":subQ1}),-1.0]])]});}
            var Q54;
            {var subQ0=sQuery(id+"F2.wireOp",EDGE,"E8.0.10.0");var subQ1=sQuery(id+"F2.wireOp",EDGE,"E1.0");var subQ2=makeQuery(id+"F2.imprint","INTERSECT",VERTEX,{"derivedFrom":[subQ1,subQ0]});Q54=makeQuery(id+"F2.imprint","IMPRINT",FACE,{"disambiguationData":[TD([[makeQuery(id+"F2.imprint","IMPRINT",EDGE,{"disambiguationData":[TD([[subQ2,-1.0]])],"derivedFrom":subQ1}),-1.0]])]});}
            var Q55;
            {var subQ0=sQuery(id+"F2.wireOp",EDGE,"E8.0.11.0");var subQ1=sQuery(id+"F2.wireOp",EDGE,"E1.0");var subQ2=makeQuery(id+"F2.imprint","INTERSECT",VERTEX,{"derivedFrom":[subQ1,subQ0]});Q55=makeQuery(id+"F2.imprint","IMPRINT",FACE,{"disambiguationData":[TD([[makeQuery(id+"F2.imprint","IMPRINT",EDGE,{"disambiguationData":[TD([[subQ2,-1.0]])],"derivedFrom":subQ1}),-1.0]])]});}
            var Q56;
            {var subQ0=sQuery(id+"F2.wireOp",EDGE,"E8.0.11.0");var subQ1=sQuery(id+"F2.wireOp",EDGE,"E2");var subQ2=makeQuery(id+"F2.imprint","INTERSECT",VERTEX,{"derivedFrom":[subQ1,subQ0]});Q56=makeQuery(id+"F2.imprint","IMPRINT",FACE,{"disambiguationData":[TD([[makeQuery(id+"F2.imprint","IMPRINT",EDGE,{"disambiguationData":[TD([[subQ2,-1.0]])],"derivedFrom":subQ1}),-1.0]])]});}
            var Q57;
            {var subQ0=sQuery(id+"F2.wireOp",EDGE,"E8.0.11.0");var subQ1=sQuery(id+"F2.wireOp",EDGE,"E7.1.0.1");var subQ2=makeQuery(id+"F2.imprint","INTERSECT",VERTEX,{"derivedFrom":[subQ1,subQ0]});Q57=makeQuery(id+"F2.imprint","IMPRINT",FACE,{"disambiguationData":[TD([[makeQuery(id+"F2.imprint","IMPRINT",EDGE,{"disambiguationData":[TD([[subQ2,-1.0]])],"derivedFrom":subQ1}),-1.0]])]});}
            var Q58;
            {var subQ0=sQuery(id+"F2.wireOp",EDGE,"E8.0.11.0");var subQ1=sQuery(id+"F2.wireOp",EDGE,"E7.2.0.1");var subQ2=makeQuery(id+"F2.imprint","INTERSECT",VERTEX,{"derivedFrom":[subQ1,subQ0]});Q58=makeQuery(id+"F2.imprint","IMPRINT",FACE,{"disambiguationData":[TD([[makeQuery(id+"F2.imprint","IMPRINT",EDGE,{"disambiguationData":[TD([[subQ2,-1.0]])],"derivedFrom":subQ1}),-1.0]])]});}
            var Q59;
            {var subQ0=sQuery(id+"F2.wireOp",EDGE,"E8.0.11.0");var subQ1=sQuery(id+"F2.wireOp",EDGE,"E7.3.0.1");var subQ2=makeQuery(id+"F2.imprint","INTERSECT",VERTEX,{"derivedFrom":[subQ1,subQ0]});Q59=makeQuery(id+"F2.imprint","IMPRINT",FACE,{"disambiguationData":[TD([[makeQuery(id+"F2.imprint","IMPRINT",EDGE,{"disambiguationData":[TD([[subQ2,-1.0]])],"derivedFrom":subQ1}),-1.0]])]});}
            var Q60;
            {var subQ0=sQuery(id+"F2.wireOp",EDGE,"E8.0.12.0");var subQ1=sQuery(id+"F2.wireOp",EDGE,"E7.3.0.1");var subQ2=makeQuery(id+"F2.imprint","INTERSECT",VERTEX,{"derivedFrom":[subQ1,subQ0]});Q60=makeQuery(id+"F2.imprint","IMPRINT",FACE,{"disambiguationData":[TD([[makeQuery(id+"F2.imprint","IMPRINT",EDGE,{"disambiguationData":[TD([[subQ2,-1.0]])],"derivedFrom":subQ1}),-1.0]])]});}
            var Q61;
            {var subQ0=sQuery(id+"F2.wireOp",EDGE,"E8.0.12.0");var subQ1=sQuery(id+"F2.wireOp",EDGE,"E7.2.0.1");var subQ2=makeQuery(id+"F2.imprint","INTERSECT",VERTEX,{"derivedFrom":[subQ1,subQ0]});Q61=makeQuery(id+"F2.imprint","IMPRINT",FACE,{"disambiguationData":[TD([[makeQuery(id+"F2.imprint","IMPRINT",EDGE,{"disambiguationData":[TD([[subQ2,-1.0]])],"derivedFrom":subQ1}),-1.0]])]});}
            var Q62;
            {var subQ0=sQuery(id+"F2.wireOp",EDGE,"E8.0.12.0");var subQ1=sQuery(id+"F2.wireOp",EDGE,"E7.1.0.1");var subQ2=makeQuery(id+"F2.imprint","INTERSECT",VERTEX,{"derivedFrom":[subQ1,subQ0]});Q62=makeQuery(id+"F2.imprint","IMPRINT",FACE,{"disambiguationData":[TD([[makeQuery(id+"F2.imprint","IMPRINT",EDGE,{"disambiguationData":[TD([[subQ2,-1.0]])],"derivedFrom":subQ1}),-1.0]])]});}
            var Q63;
            {var subQ0=sQuery(id+"F2.wireOp",EDGE,"E8.0.12.0");var subQ1=sQuery(id+"F2.wireOp",EDGE,"E2");var subQ2=makeQuery(id+"F2.imprint","INTERSECT",VERTEX,{"derivedFrom":[subQ1,subQ0]});Q63=makeQuery(id+"F2.imprint","IMPRINT",FACE,{"disambiguationData":[TD([[makeQuery(id+"F2.imprint","IMPRINT",EDGE,{"disambiguationData":[TD([[subQ2,-1.0]])],"derivedFrom":subQ1}),-1.0]])]});}
            var Q64;
            {var subQ0=sQuery(id+"F2.wireOp",EDGE,"E8.0.12.0");var subQ1=sQuery(id+"F2.wireOp",EDGE,"E1.0");var subQ2=makeQuery(id+"F2.imprint","INTERSECT",VERTEX,{"derivedFrom":[subQ1,subQ0]});Q64=makeQuery(id+"F2.imprint","IMPRINT",FACE,{"disambiguationData":[TD([[makeQuery(id+"F2.imprint","IMPRINT",EDGE,{"disambiguationData":[TD([[subQ2,-1.0]])],"derivedFrom":subQ1}),-1.0]])]});}
            var Q65;
            {var subQ0=sQuery(id+"F2.wireOp",EDGE,"E8.0.13.0");var subQ1=sQuery(id+"F2.wireOp",EDGE,"E1.0");var subQ2=makeQuery(id+"F2.imprint","INTERSECT",VERTEX,{"derivedFrom":[subQ1,subQ0]});Q65=makeQuery(id+"F2.imprint","IMPRINT",FACE,{"disambiguationData":[TD([[makeQuery(id+"F2.imprint","IMPRINT",EDGE,{"disambiguationData":[TD([[subQ2,-1.0]])],"derivedFrom":subQ1}),-1.0]])]});}
            var Q66;
            {var subQ0=sQuery(id+"F2.wireOp",EDGE,"E8.0.13.0");var subQ1=sQuery(id+"F2.wireOp",EDGE,"E2");var subQ2=makeQuery(id+"F2.imprint","INTERSECT",VERTEX,{"derivedFrom":[subQ1,subQ0]});Q66=makeQuery(id+"F2.imprint","IMPRINT",FACE,{"disambiguationData":[TD([[makeQuery(id+"F2.imprint","IMPRINT",EDGE,{"disambiguationData":[TD([[subQ2,-1.0]])],"derivedFrom":subQ1}),-1.0]])]});}
            var Q67;
            {var subQ0=sQuery(id+"F2.wireOp",EDGE,"E8.0.13.0");var subQ1=sQuery(id+"F2.wireOp",EDGE,"E7.1.0.1");var subQ2=makeQuery(id+"F2.imprint","INTERSECT",VERTEX,{"derivedFrom":[subQ1,subQ0]});Q67=makeQuery(id+"F2.imprint","IMPRINT",FACE,{"disambiguationData":[TD([[makeQuery(id+"F2.imprint","IMPRINT",EDGE,{"disambiguationData":[TD([[subQ2,-1.0]])],"derivedFrom":subQ1}),-1.0]])]});}
            var Q68;
            {var subQ0=sQuery(id+"F2.wireOp",EDGE,"E8.0.13.0");var subQ1=sQuery(id+"F2.wireOp",EDGE,"E7.2.0.1");var subQ2=makeQuery(id+"F2.imprint","INTERSECT",VERTEX,{"derivedFrom":[subQ1,subQ0]});Q68=makeQuery(id+"F2.imprint","IMPRINT",FACE,{"disambiguationData":[TD([[makeQuery(id+"F2.imprint","IMPRINT",EDGE,{"disambiguationData":[TD([[subQ2,-1.0]])],"derivedFrom":subQ1}),-1.0]])]});}
            var Q69;
            {var subQ0=sQuery(id+"F2.wireOp",EDGE,"E8.0.13.0");var subQ1=sQuery(id+"F2.wireOp",EDGE,"E7.3.0.1");var subQ2=makeQuery(id+"F2.imprint","INTERSECT",VERTEX,{"derivedFrom":[subQ1,subQ0]});Q69=makeQuery(id+"F2.imprint","IMPRINT",FACE,{"disambiguationData":[TD([[makeQuery(id+"F2.imprint","IMPRINT",EDGE,{"disambiguationData":[TD([[subQ2,-1.0]])],"derivedFrom":subQ1}),-1.0]])]});}
            var Q70;
            {var subQ0=sQuery(id+"F2.wireOp",EDGE,"E8.0.14.0");var subQ1=sQuery(id+"F2.wireOp",EDGE,"E7.3.0.1");var subQ2=makeQuery(id+"F2.imprint","INTERSECT",VERTEX,{"derivedFrom":[subQ1,subQ0]});Q70=makeQuery(id+"F2.imprint","IMPRINT",FACE,{"disambiguationData":[TD([[makeQuery(id+"F2.imprint","IMPRINT",EDGE,{"disambiguationData":[TD([[subQ2,-1.0]])],"derivedFrom":subQ1}),-1.0]])]});}
            var Q71;
            {var subQ0=sQuery(id+"F2.wireOp",EDGE,"E8.0.14.0");var subQ1=sQuery(id+"F2.wireOp",EDGE,"E7.2.0.1");var subQ2=makeQuery(id+"F2.imprint","INTERSECT",VERTEX,{"derivedFrom":[subQ1,subQ0]});Q71=makeQuery(id+"F2.imprint","IMPRINT",FACE,{"disambiguationData":[TD([[makeQuery(id+"F2.imprint","IMPRINT",EDGE,{"disambiguationData":[TD([[subQ2,-1.0]])],"derivedFrom":subQ1}),-1.0]])]});}
            var Q72;
            {var subQ0=sQuery(id+"F2.wireOp",EDGE,"E8.0.14.0");var subQ1=sQuery(id+"F2.wireOp",EDGE,"E7.1.0.1");var subQ2=makeQuery(id+"F2.imprint","INTERSECT",VERTEX,{"derivedFrom":[subQ1,subQ0]});Q72=makeQuery(id+"F2.imprint","IMPRINT",FACE,{"disambiguationData":[TD([[makeQuery(id+"F2.imprint","IMPRINT",EDGE,{"disambiguationData":[TD([[subQ2,-1.0]])],"derivedFrom":subQ1}),-1.0]])]});}
            var Q73;
            {var subQ0=sQuery(id+"F2.wireOp",EDGE,"E8.0.14.0");var subQ1=sQuery(id+"F2.wireOp",EDGE,"E2");var subQ2=makeQuery(id+"F2.imprint","INTERSECT",VERTEX,{"derivedFrom":[subQ1,subQ0]});Q73=makeQuery(id+"F2.imprint","IMPRINT",FACE,{"disambiguationData":[TD([[makeQuery(id+"F2.imprint","IMPRINT",EDGE,{"disambiguationData":[TD([[subQ2,-1.0]])],"derivedFrom":subQ1}),-1.0]])]});}
            var Q74;
            {var subQ0=sQuery(id+"F2.wireOp",EDGE,"E8.0.14.0");var subQ1=sQuery(id+"F2.wireOp",EDGE,"E1.0");var subQ2=makeQuery(id+"F2.imprint","INTERSECT",VERTEX,{"derivedFrom":[subQ1,subQ0]});Q74=makeQuery(id+"F2.imprint","IMPRINT",FACE,{"disambiguationData":[TD([[makeQuery(id+"F2.imprint","IMPRINT",EDGE,{"disambiguationData":[TD([[subQ2,-1.0]])],"derivedFrom":subQ1}),-1.0]])]});}
            var Q75;
            {var subQ0=sQuery(id+"F2.wireOp",EDGE,"E8.0.15.0");var subQ1=sQuery(id+"F2.wireOp",EDGE,"E1.0");var subQ2=makeQuery(id+"F2.imprint","INTERSECT",VERTEX,{"derivedFrom":[subQ1,subQ0]});Q75=makeQuery(id+"F2.imprint","IMPRINT",FACE,{"disambiguationData":[TD([[makeQuery(id+"F2.imprint","IMPRINT",EDGE,{"disambiguationData":[TD([[subQ2,-1.0]])],"derivedFrom":subQ1}),-1.0]])]});}
            var Q76;
            {var subQ0=sQuery(id+"F2.wireOp",EDGE,"E8.0.15.0");var subQ1=sQuery(id+"F2.wireOp",EDGE,"E2");var subQ2=makeQuery(id+"F2.imprint","INTERSECT",VERTEX,{"derivedFrom":[subQ1,subQ0]});Q76=makeQuery(id+"F2.imprint","IMPRINT",FACE,{"disambiguationData":[TD([[makeQuery(id+"F2.imprint","IMPRINT",EDGE,{"disambiguationData":[TD([[subQ2,-1.0]])],"derivedFrom":subQ1}),-1.0]])]});}
            var Q77;
            {var subQ0=sQuery(id+"F2.wireOp",EDGE,"E8.0.15.0");var subQ1=sQuery(id+"F2.wireOp",EDGE,"E7.1.0.1");var subQ2=makeQuery(id+"F2.imprint","INTERSECT",VERTEX,{"derivedFrom":[subQ1,subQ0]});Q77=makeQuery(id+"F2.imprint","IMPRINT",FACE,{"disambiguationData":[TD([[makeQuery(id+"F2.imprint","IMPRINT",EDGE,{"disambiguationData":[TD([[subQ2,-1.0]])],"derivedFrom":subQ1}),-1.0]])]});}
            var Q78;
            {var subQ0=sQuery(id+"F2.wireOp",EDGE,"E8.0.15.0");var subQ1=sQuery(id+"F2.wireOp",EDGE,"E7.2.0.1");var subQ2=makeQuery(id+"F2.imprint","INTERSECT",VERTEX,{"derivedFrom":[subQ1,subQ0]});Q78=makeQuery(id+"F2.imprint","IMPRINT",FACE,{"disambiguationData":[TD([[makeQuery(id+"F2.imprint","IMPRINT",EDGE,{"disambiguationData":[TD([[subQ2,-1.0]])],"derivedFrom":subQ1}),-1.0]])]});}
            var Q79;
            {var subQ0=sQuery(id+"F2.wireOp",EDGE,"E8.0.15.0");var subQ1=sQuery(id+"F2.wireOp",EDGE,"E7.3.0.1");var subQ2=makeQuery(id+"F2.imprint","INTERSECT",VERTEX,{"derivedFrom":[subQ1,subQ0]});Q79=makeQuery(id+"F2.imprint","IMPRINT",FACE,{"disambiguationData":[TD([[makeQuery(id+"F2.imprint","IMPRINT",EDGE,{"disambiguationData":[TD([[subQ2,-1.0]])],"derivedFrom":subQ1}),-1.0]])]});}
            var Q80;
            {var subQ0=sQuery(id+"F2.wireOp",EDGE,"E8.0.16.0");var subQ1=sQuery(id+"F2.wireOp",EDGE,"E7.3.0.1");var subQ2=makeQuery(id+"F2.imprint","INTERSECT",VERTEX,{"derivedFrom":[subQ1,subQ0]});Q80=makeQuery(id+"F2.imprint","IMPRINT",FACE,{"disambiguationData":[TD([[makeQuery(id+"F2.imprint","IMPRINT",EDGE,{"disambiguationData":[TD([[subQ2,-1.0]])],"derivedFrom":subQ1}),-1.0]])]});}
            var Q81;
            {var subQ0=sQuery(id+"F2.wireOp",EDGE,"E8.0.16.0");var subQ1=sQuery(id+"F2.wireOp",EDGE,"E7.2.0.1");var subQ2=makeQuery(id+"F2.imprint","INTERSECT",VERTEX,{"derivedFrom":[subQ1,subQ0]});Q81=makeQuery(id+"F2.imprint","IMPRINT",FACE,{"disambiguationData":[TD([[makeQuery(id+"F2.imprint","IMPRINT",EDGE,{"disambiguationData":[TD([[subQ2,-1.0]])],"derivedFrom":subQ1}),-1.0]])]});}
            var Q82;
            {var subQ0=sQuery(id+"F2.wireOp",EDGE,"E8.0.16.0");var subQ1=sQuery(id+"F2.wireOp",EDGE,"E7.1.0.1");var subQ2=makeQuery(id+"F2.imprint","INTERSECT",VERTEX,{"derivedFrom":[subQ1,subQ0]});Q82=makeQuery(id+"F2.imprint","IMPRINT",FACE,{"disambiguationData":[TD([[makeQuery(id+"F2.imprint","IMPRINT",EDGE,{"disambiguationData":[TD([[subQ2,-1.0]])],"derivedFrom":subQ1}),-1.0]])]});}
            var Q83;
            {var subQ0=sQuery(id+"F2.wireOp",EDGE,"E8.0.16.0");var subQ1=sQuery(id+"F2.wireOp",EDGE,"E2");var subQ2=makeQuery(id+"F2.imprint","INTERSECT",VERTEX,{"derivedFrom":[subQ1,subQ0]});Q83=makeQuery(id+"F2.imprint","IMPRINT",FACE,{"disambiguationData":[TD([[makeQuery(id+"F2.imprint","IMPRINT",EDGE,{"disambiguationData":[TD([[subQ2,-1.0]])],"derivedFrom":subQ1}),-1.0]])]});}
            var Q84;
            {var subQ0=sQuery(id+"F2.wireOp",EDGE,"E8.0.16.0");var subQ1=sQuery(id+"F2.wireOp",EDGE,"E1.0");var subQ2=makeQuery(id+"F2.imprint","INTERSECT",VERTEX,{"derivedFrom":[subQ1,subQ0]});Q84=makeQuery(id+"F2.imprint","IMPRINT",FACE,{"disambiguationData":[TD([[makeQuery(id+"F2.imprint","IMPRINT",EDGE,{"disambiguationData":[TD([[subQ2,-1.0]])],"derivedFrom":subQ1}),-1.0]])]});}
            var Q85;
            {var subQ0=sQuery(id+"F2.wireOp",EDGE,"E8.0.17.0");var subQ1=sQuery(id+"F2.wireOp",EDGE,"E1.0");var subQ2=makeQuery(id+"F2.imprint","INTERSECT",VERTEX,{"derivedFrom":[subQ1,subQ0]});Q85=makeQuery(id+"F2.imprint","IMPRINT",FACE,{"disambiguationData":[TD([[makeQuery(id+"F2.imprint","IMPRINT",EDGE,{"disambiguationData":[TD([[subQ2,-1.0]])],"derivedFrom":subQ1}),-1.0]])]});}
            var Q86;
            {var subQ0=sQuery(id+"F2.wireOp",EDGE,"E8.0.17.0");var subQ1=sQuery(id+"F2.wireOp",EDGE,"E2");var subQ2=makeQuery(id+"F2.imprint","INTERSECT",VERTEX,{"derivedFrom":[subQ1,subQ0]});Q86=makeQuery(id+"F2.imprint","IMPRINT",FACE,{"disambiguationData":[TD([[makeQuery(id+"F2.imprint","IMPRINT",EDGE,{"disambiguationData":[TD([[subQ2,-1.0]])],"derivedFrom":subQ1}),-1.0]])]});}
            var Q87;
            {var subQ0=sQuery(id+"F2.wireOp",EDGE,"E8.0.17.0");var subQ1=sQuery(id+"F2.wireOp",EDGE,"E7.1.0.1");var subQ2=makeQuery(id+"F2.imprint","INTERSECT",VERTEX,{"derivedFrom":[subQ1,subQ0]});Q87=makeQuery(id+"F2.imprint","IMPRINT",FACE,{"disambiguationData":[TD([[makeQuery(id+"F2.imprint","IMPRINT",EDGE,{"disambiguationData":[TD([[subQ2,-1.0]])],"derivedFrom":subQ1}),-1.0]])]});}
            var Q88;
            {var subQ0=sQuery(id+"F2.wireOp",EDGE,"E8.0.17.0");var subQ1=sQuery(id+"F2.wireOp",EDGE,"E7.2.0.1");var subQ2=makeQuery(id+"F2.imprint","INTERSECT",VERTEX,{"derivedFrom":[subQ1,subQ0]});Q88=makeQuery(id+"F2.imprint","IMPRINT",FACE,{"disambiguationData":[TD([[makeQuery(id+"F2.imprint","IMPRINT",EDGE,{"disambiguationData":[TD([[subQ2,-1.0]])],"derivedFrom":subQ1}),-1.0]])]});}
            var Q89;
            {var subQ0=sQuery(id+"F2.wireOp",EDGE,"E8.0.17.0");var subQ1=sQuery(id+"F2.wireOp",EDGE,"E7.3.0.1");var subQ2=makeQuery(id+"F2.imprint","INTERSECT",VERTEX,{"derivedFrom":[subQ1,subQ0]});Q89=makeQuery(id+"F2.imprint","IMPRINT",FACE,{"disambiguationData":[TD([[makeQuery(id+"F2.imprint","IMPRINT",EDGE,{"disambiguationData":[TD([[subQ2,-1.0]])],"derivedFrom":subQ1}),-1.0]])]});}
            var Q90;
            {var subQ0=sQuery(id+"F2.wireOp",EDGE,"E7.3.0.1");var subQ1=makeQuery(id+"F1.opExtrude","CAP_EDGE",EDGE,{"disambiguationData":[OSD([sQuery(id+"F0.wireOp",EDGE,"E0.top")])],"isStart":false});var subQ2=makeQuery(id+"F2.imprint","INTERSECT",VERTEX,{"derivedFrom":[subQ1,subQ0]});Q90=makeQuery(id+"F2.imprint","IMPRINT",FACE,{"disambiguationData":[TD([[makeQuery(id+"F2.imprint","IMPRINT",EDGE,{"disambiguationData":[TD([[subQ2,1.0]])],"derivedFrom":subQ0}),-1.0]])]});}
            var Q91;
            {var subQ0=sQuery(id+"F2.wireOp",EDGE,"E7.2.0.1");var subQ1=makeQuery(id+"F1.opExtrude","CAP_EDGE",EDGE,{"disambiguationData":[OSD([sQuery(id+"F0.wireOp",EDGE,"E0.top")])],"isStart":false});var subQ2=makeQuery(id+"F2.imprint","INTERSECT",VERTEX,{"derivedFrom":[subQ1,subQ0]});Q91=makeQuery(id+"F2.imprint","IMPRINT",FACE,{"disambiguationData":[TD([[makeQuery(id+"F2.imprint","IMPRINT",EDGE,{"disambiguationData":[TD([[subQ2,1.0]])],"derivedFrom":subQ0}),-1.0]])]});}
            var Q92;
            {var subQ0=sQuery(id+"F2.wireOp",EDGE,"E7.1.0.1");var subQ1=makeQuery(id+"F1.opExtrude","CAP_EDGE",EDGE,{"disambiguationData":[OSD([sQuery(id+"F0.wireOp",EDGE,"E0.top")])],"isStart":false});var subQ2=makeQuery(id+"F2.imprint","INTERSECT",VERTEX,{"derivedFrom":[subQ1,subQ0]});Q92=makeQuery(id+"F2.imprint","IMPRINT",FACE,{"disambiguationData":[TD([[makeQuery(id+"F2.imprint","IMPRINT",EDGE,{"disambiguationData":[TD([[subQ2,1.0]])],"derivedFrom":subQ0}),-1.0]])]});}
            var Q93;
            {var subQ0=sQuery(id+"F2.wireOp",EDGE,"E2");var subQ1=makeQuery(id+"F1.opExtrude","CAP_EDGE",EDGE,{"disambiguationData":[OSD([sQuery(id+"F0.wireOp",EDGE,"E0.top")])],"isStart":false});var subQ2=makeQuery(id+"F2.imprint","INTERSECT",VERTEX,{"derivedFrom":[subQ1,subQ0]});Q93=makeQuery(id+"F2.imprint","IMPRINT",FACE,{"disambiguationData":[TD([[makeQuery(id+"F2.imprint","IMPRINT",EDGE,{"disambiguationData":[TD([[subQ2,1.0]])],"derivedFrom":subQ0}),-1.0]])]});}
            var Q94;
            {var subQ0=sQuery(id+"F2.wireOp",EDGE,"E1.0");var subQ1=makeQuery(id+"F1.opExtrude","CAP_EDGE",EDGE,{"disambiguationData":[OSD([sQuery(id+"F0.wireOp",EDGE,"E0.top")])],"isStart":false});var subQ2=makeQuery(id+"F2.imprint","INTERSECT",VERTEX,{"derivedFrom":[subQ1,subQ0]});Q94=makeQuery(id+"F2.imprint","IMPRINT",FACE,{"disambiguationData":[TD([[makeQuery(id+"F2.imprint","IMPRINT",EDGE,{"disambiguationData":[TD([[subQ2,1.0]])],"derivedFrom":subQ0}),-1.0]])]});}
            var Q95;
            {var subQ0=sQuery(id+"F2.wireOp",EDGE,"E6.0");var subQ1=sQuery(id+"F2.wireOp",EDGE,"E1.0");var subQ2=makeQuery(id+"F2.imprint","INTERSECT",VERTEX,{"derivedFrom":[subQ1,subQ0]});Q95=makeQuery(id+"F2.imprint","IMPRINT",FACE,{"disambiguationData":[TD([[makeQuery(id+"F2.imprint","IMPRINT",EDGE,{"disambiguationData":[TD([[subQ2,1.0]])],"derivedFrom":subQ1}),-1.0]])]});}
            var Q96;
            {var subQ0=sQuery(id+"F2.wireOp",EDGE,"E3.0");var subQ1=sQuery(id+"F2.wireOp",EDGE,"E2");var subQ2=makeQuery(id+"F2.imprint","INTERSECT",VERTEX,{"derivedFrom":[subQ1,subQ0]});Q96=makeQuery(id+"F2.imprint","IMPRINT",FACE,{"disambiguationData":[TD([[makeQuery(id+"F2.imprint","IMPRINT",EDGE,{"disambiguationData":[TD([[subQ2,-1.0]])],"derivedFrom":subQ1}),-1.0]])]});}
            var Q97;
            {var subQ0=sQuery(id+"F2.wireOp",EDGE,"E7.1.0.1");var subQ1=sQuery(id+"F2.wireOp",EDGE,"E3.0");var subQ2=makeQuery(id+"F2.imprint","INTERSECT",VERTEX,{"derivedFrom":[subQ1,subQ0]});Q97=makeQuery(id+"F2.imprint","IMPRINT",FACE,{"disambiguationData":[TD([[makeQuery(id+"F2.imprint","IMPRINT",EDGE,{"disambiguationData":[TD([[subQ2,-1.0]])],"derivedFrom":subQ1}),1.0]])]});}
            var Q98;
            {var subQ0=sQuery(id+"F2.wireOp",EDGE,"E7.2.0.1");var subQ1=sQuery(id+"F2.wireOp",EDGE,"E3.0");var subQ2=makeQuery(id+"F2.imprint","INTERSECT",VERTEX,{"derivedFrom":[subQ1,subQ0]});Q98=makeQuery(id+"F2.imprint","IMPRINT",FACE,{"disambiguationData":[TD([[makeQuery(id+"F2.imprint","IMPRINT",EDGE,{"disambiguationData":[TD([[subQ2,-1.0]])],"derivedFrom":subQ1}),1.0]])]});}
            var Q99;
            {var subQ0=sQuery(id+"F2.wireOp",EDGE,"E3.0");var subQ1=makeQuery(id+"F1.opExtrude","CAP_EDGE",EDGE,{"disambiguationData":[OSD([sQuery(id+"F0.wireOp",EDGE,"E0.right")])],"isStart":false});var subQ2=makeQuery(id+"F2.imprint","INTERSECT",VERTEX,{"derivedFrom":[subQ1,subQ0]});Q99=makeQuery(id+"F2.imprint","IMPRINT",FACE,{"disambiguationData":[TD([[makeQuery(id+"F2.imprint","IMPRINT",EDGE,{"disambiguationData":[TD([[subQ2,1.0]])],"derivedFrom":subQ0}),1.0]])]});}
            extrude(context, id + "F3", {"entities" : qUnion([Q0, Q1, Q2, Q3, Q4, Q5, Q6, Q7, Q8, Q9, Q10, Q11, Q12, Q13, Q14, Q15, Q16, Q17, Q18, Q19, Q20, Q21, Q22, Q23, Q24, Q25, Q26, Q27, Q28, Q29, Q30, Q31, Q32, Q33, Q34, Q35, Q36, Q37, Q38, Q39, Q40, Q41, Q42, Q43, Q44, Q45, Q46, Q47, Q48, Q49, Q50, Q51, Q52, Q53, Q54, Q55, Q56, Q57, Q58, Q59, Q60, Q61, Q62, Q63, Q64, Q65, Q66, Q67, Q68, Q69, Q70, Q71, Q72, Q73, Q74, Q75, Q76, Q77, Q78, Q79, Q80, Q81, Q82, Q83, Q84, Q85, Q86, Q87, Q88, Q89, Q90, Q91, Q92, Q93, Q94, Q95, Q96, Q97, Q98, Q99]), "operationType" : NewBodyOperationType.ADD, "depth" : 0 * mm, "offsetDistance" : 25.4 * mm});
        }
    });
